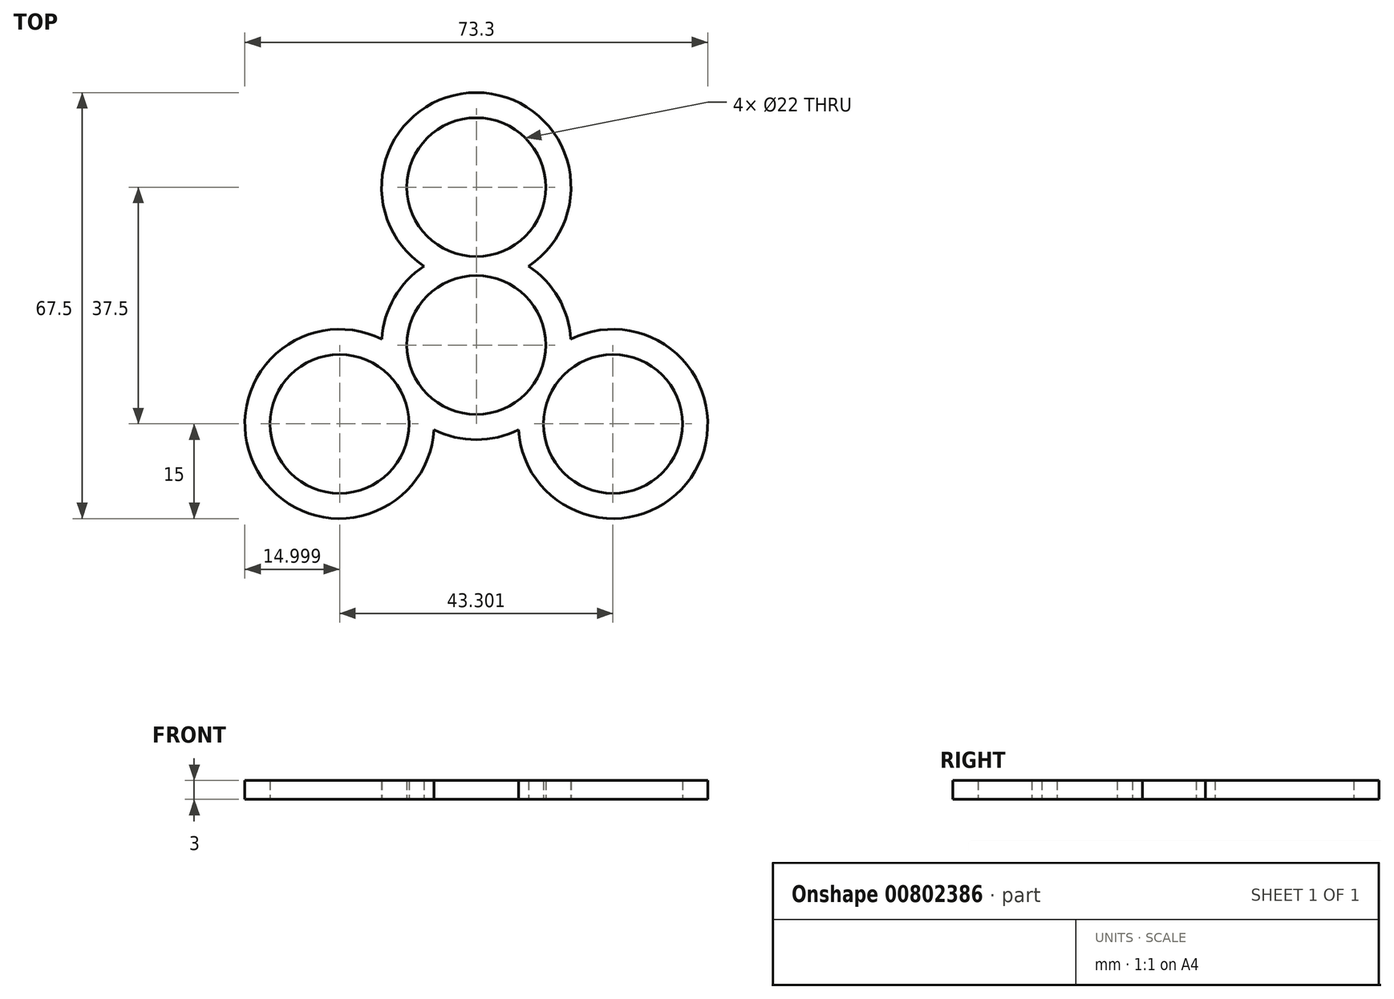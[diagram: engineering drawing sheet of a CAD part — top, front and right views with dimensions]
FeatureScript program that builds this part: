
annotation { "Feature Type Name" : "Feature", "Feature Type Description" : "" }
export const myFeature = defineFeature(function(context is Context, id is Id, definition is map)
    precondition{}
    {
        {
            var Q0;
            Q0=qCreatedBy(makeId("Top.planeOp"),FACE);
            var sketch = newSketch(context, id + "F0", { "sketchPlane" : qUnion([Q0])});
            skArc(sketch, "E0", {"start": v(9.53, 5.5) * mm, "mid": v(0, 11) * mm, "end": v(-9.53, 5.5) * mm});
            skCircle(sketch, "E1", {"center": v(0, 25) * mm, "radius": 11 * mm});
            skArc(sketch, "E2", {"start": v(8.3, 12.5) * mm, "mid": v(0, 40) * mm, "end": v(-8.3, 12.5) * mm});
            skArc(sketch, "E3", {"start": v(13, 7.5) * mm, "mid": v(10.93, 10.27) * mm, "end": v(8.3, 12.5) * mm});
            skArc(sketch, "E4.trimOffspring", {"start": v(-8.3, 12.5) * mm, "mid": v(-10.93, 10.27) * mm, "end": v(-13, 7.5) * mm});
            skArc(sketch, "E5.1.0", {"start": v(-14.97, 0.93) * mm, "mid": v(-34.64, -20) * mm, "end": v(-6.68, -13.43) * mm});
            skCircle(sketch, "E5.1.1", {"center": v(-21.65, -12.5) * mm, "radius": 11 * mm});
            skArc(sketch, "E5.1.2", {"start": v(-13, 7.5) * mm, "mid": v(-14.36, 4.33) * mm, "end": v(-14.97, 0.93) * mm});
            skArc(sketch, "E5.1.3", {"start": v(-9.53, 5.5) * mm, "mid": v(-9.53, -5.5) * mm, "end": v(0, -11) * mm});
            skArc(sketch, "E5.1.4", {"start": v(-6.68, -13.43) * mm, "mid": v(-3.43, -14.6) * mm, "end": v(0, -15) * mm});
            skArc(sketch, "E5.2.0", {"start": v(6.68, -13.43) * mm, "mid": v(34.64, -20) * mm, "end": v(14.97, 0.93) * mm});
            skCircle(sketch, "E5.2.1", {"center": v(21.65, -12.5) * mm, "radius": 11 * mm});
            skArc(sketch, "E5.2.2", {"start": v(0, -15) * mm, "mid": v(3.43, -14.6) * mm, "end": v(6.68, -13.43) * mm});
            skArc(sketch, "E5.2.3", {"start": v(0, -11) * mm, "mid": v(9.53, -5.5) * mm, "end": v(9.53, 5.5) * mm});
            skArc(sketch, "E5.2.4", {"start": v(14.97, 0.93) * mm, "mid": v(14.36, 4.33) * mm, "end": v(13, 7.5) * mm});
            skSolve(sketch);
        }
        {
            var Q0;
            Q0 = qSketchRegion(id + "F0", true);
            extrude(context, id + "F1", {"entities" : qUnion([Q0]), "depth" : 3 * mm, "offsetDistance" : 25 * mm});
        }
    });
